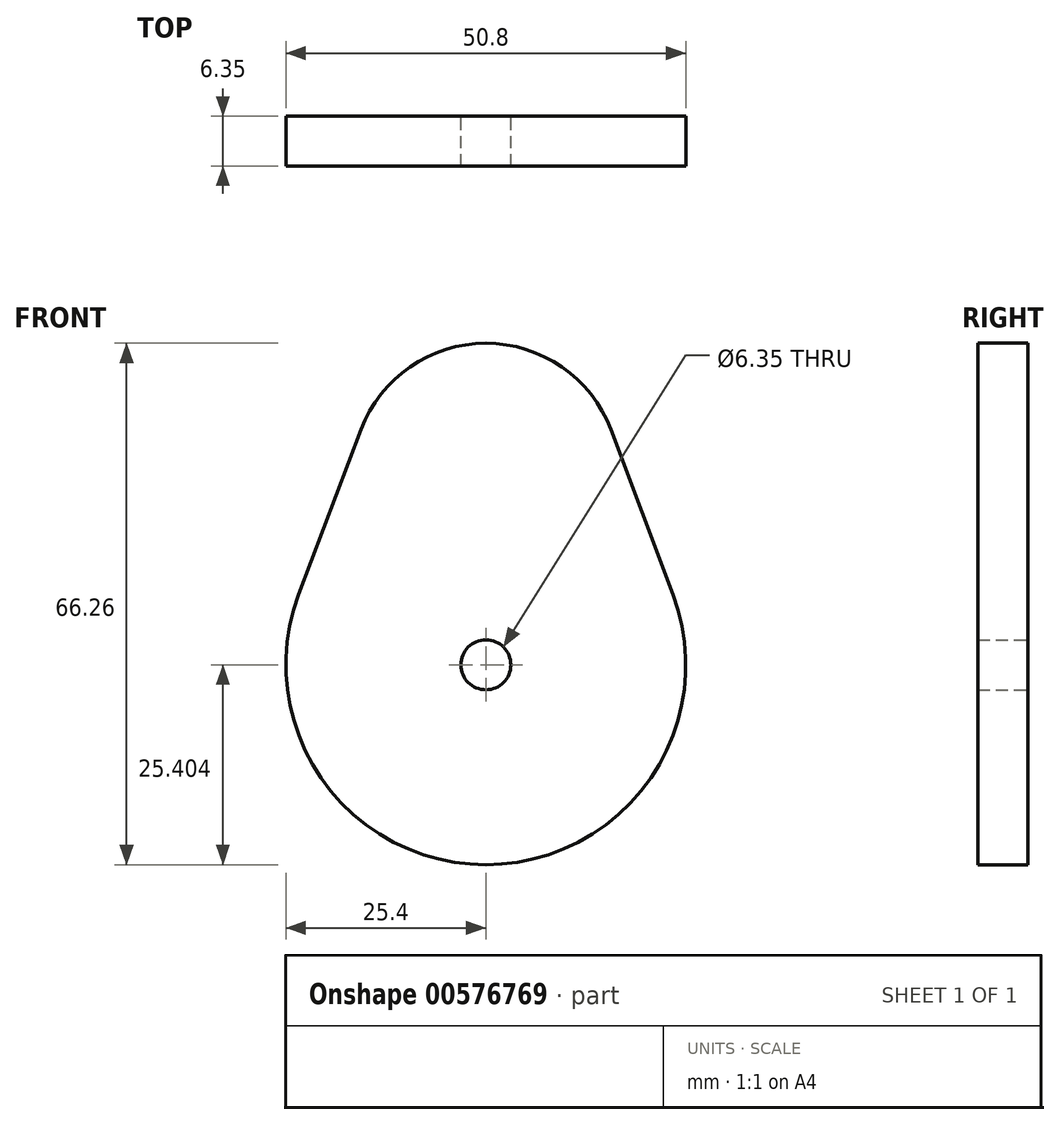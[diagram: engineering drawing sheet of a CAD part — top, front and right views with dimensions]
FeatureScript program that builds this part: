
annotation { "Feature Type Name" : "Feature", "Feature Type Description" : "" }
export const myFeature = defineFeature(function(context is Context, id is Id, definition is map)
    precondition{}
    {
        {
            var Q0;
            Q0=qCreatedBy(makeId("Front.planeOp"),FACE);
            var sketch = newSketch(context, id + "F0", { "sketchPlane" : qUnion([Q0])});
            skArc(sketch, "E0", {"start": v(-23.76, -20.9) * mm, "mid": v(0, -55.28) * mm, "end": v(23.76, -20.9) * mm});
            skLineSegment(sketch, "E1", {"start": v(-15.87, 0) * mm, "end": v(-23.76, -20.9) * mm});
            skLineSegment(sketch, "E2", {"start": v(15.87, 0) * mm, "end": v(23.76, -20.9) * mm});
            skArc(sketch, "E3", {"start": v(15.88, 0) * mm, "mid": v(0, 10.98) * mm, "end": v(-15.88, 0) * mm});
            skCircle(sketch, "E4", {"center": v(0, -29.88) * mm, "radius": 3.18 * mm});
            skSolve(sketch);
        }
        {
            var Q0;
            Q0=makeQuery(id+"F0.imprint","IMPRINT",FACE,{"disambiguationData":[TD([[makeQuery(id+"F0.imprint","IMPRINT",EDGE,{"derivedFrom":sQuery(id+"F0.wireOp",EDGE,"E0")}),1.0]])]});
            extrude(context, id + "F1", {"entities" : qUnion([Q0]), "depth" : 6.35 * mm, "offsetDistance" : 25.4 * mm});
        }
    });
